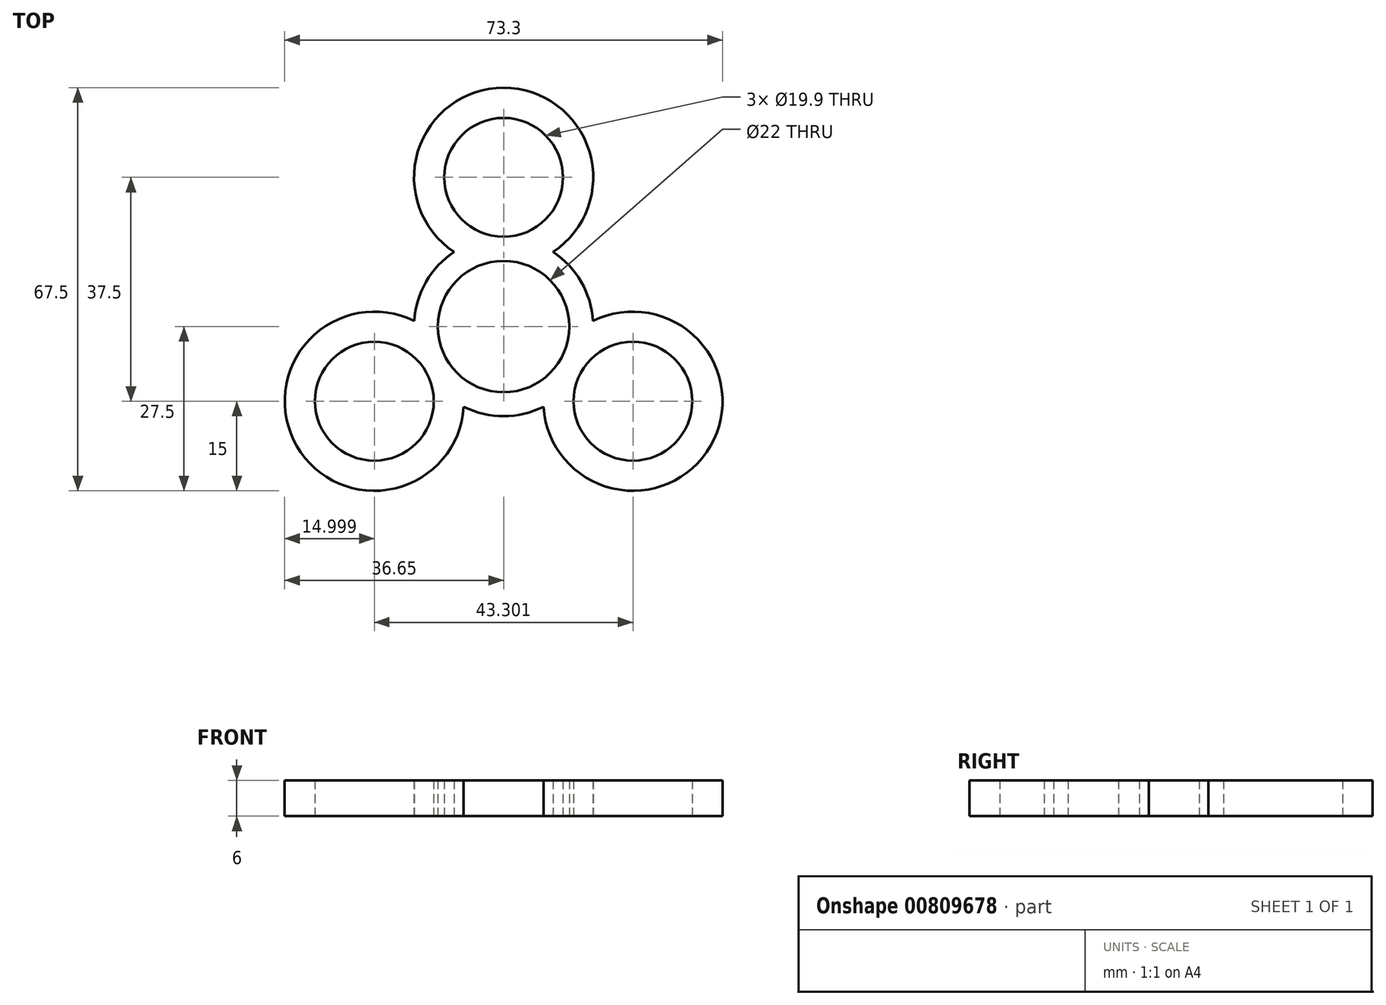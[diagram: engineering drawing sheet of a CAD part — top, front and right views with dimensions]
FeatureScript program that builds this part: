
annotation { "Feature Type Name" : "Feature", "Feature Type Description" : "" }
export const myFeature = defineFeature(function(context is Context, id is Id, definition is map)
    precondition{}
    {
        {
            var Q0;
            Q0=qCreatedBy(makeId("Top.planeOp"),FACE);
            var sketch = newSketch(context, id + "F0", { "sketchPlane" : qUnion([Q0])});
            skArc(sketch, "E0", {"start": v(9.53, 5.5) * mm, "mid": v(0, 11) * mm, "end": v(-9.53, 5.5) * mm});
            skLineSegment(sketch, "E1", {"start": v(0, 0) * mm, "end": v(0, 11) * mm});
            skCircle(sketch, "E2", {"center": v(0, 25) * mm, "radius": 9.95 * mm});
            skArc(sketch, "E3", {"start": v(13, 7.5) * mm, "mid": v(10.93, 10.27) * mm, "end": v(8.3, 12.5) * mm});
            skArc(sketch, "E4.trimOffspring", {"start": v(8.3, 12.5) * mm, "mid": v(0, 40) * mm, "end": v(-8.3, 12.5) * mm});
            skArc(sketch, "E5.trimOffspring", {"start": v(-8.3, 12.5) * mm, "mid": v(-10.93, 10.27) * mm, "end": v(-13, 7.5) * mm});
            skLineSegment(sketch, "E6.trimOffspring", {"start": v(0, 15.05) * mm, "end": v(0, 25) * mm});
            skArc(sketch, "E7.1.0", {"start": v(-14.97, 0.93) * mm, "mid": v(-34.64, -20) * mm, "end": v(-6.68, -13.43) * mm});
            skCircle(sketch, "E7.1.1", {"center": v(-21.65, -12.5) * mm, "radius": 9.95 * mm});
            skArc(sketch, "E7.1.2", {"start": v(-6.68, -13.43) * mm, "mid": v(-3.43, -14.6) * mm, "end": v(0, -15) * mm});
            skArc(sketch, "E7.1.3", {"start": v(-9.53, 5.5) * mm, "mid": v(-9.53, -5.5) * mm, "end": v(0, -11) * mm});
            skArc(sketch, "E7.1.4", {"start": v(-13, 7.5) * mm, "mid": v(-14.36, 4.33) * mm, "end": v(-14.97, 0.93) * mm});
            skArc(sketch, "E7.2.0", {"start": v(6.68, -13.43) * mm, "mid": v(34.64, -20) * mm, "end": v(14.97, 0.93) * mm});
            skCircle(sketch, "E7.2.1", {"center": v(21.65, -12.5) * mm, "radius": 9.95 * mm});
            skArc(sketch, "E7.2.2", {"start": v(14.97, 0.93) * mm, "mid": v(14.36, 4.33) * mm, "end": v(13, 7.5) * mm});
            skArc(sketch, "E7.2.3", {"start": v(0, -11) * mm, "mid": v(9.53, -5.5) * mm, "end": v(9.53, 5.5) * mm});
            skArc(sketch, "E7.2.4", {"start": v(0, -15) * mm, "mid": v(3.43, -14.6) * mm, "end": v(6.68, -13.43) * mm});
            skSolve(sketch);
        }
        {
            var Q0;
            Q0 = qSketchRegion(id + "F0", true);
            extrude(context, id + "F1", {"entities" : qUnion([Q0]), "depth" : 6 * mm, "offsetDistance" : 25 * mm});
        }
    });
